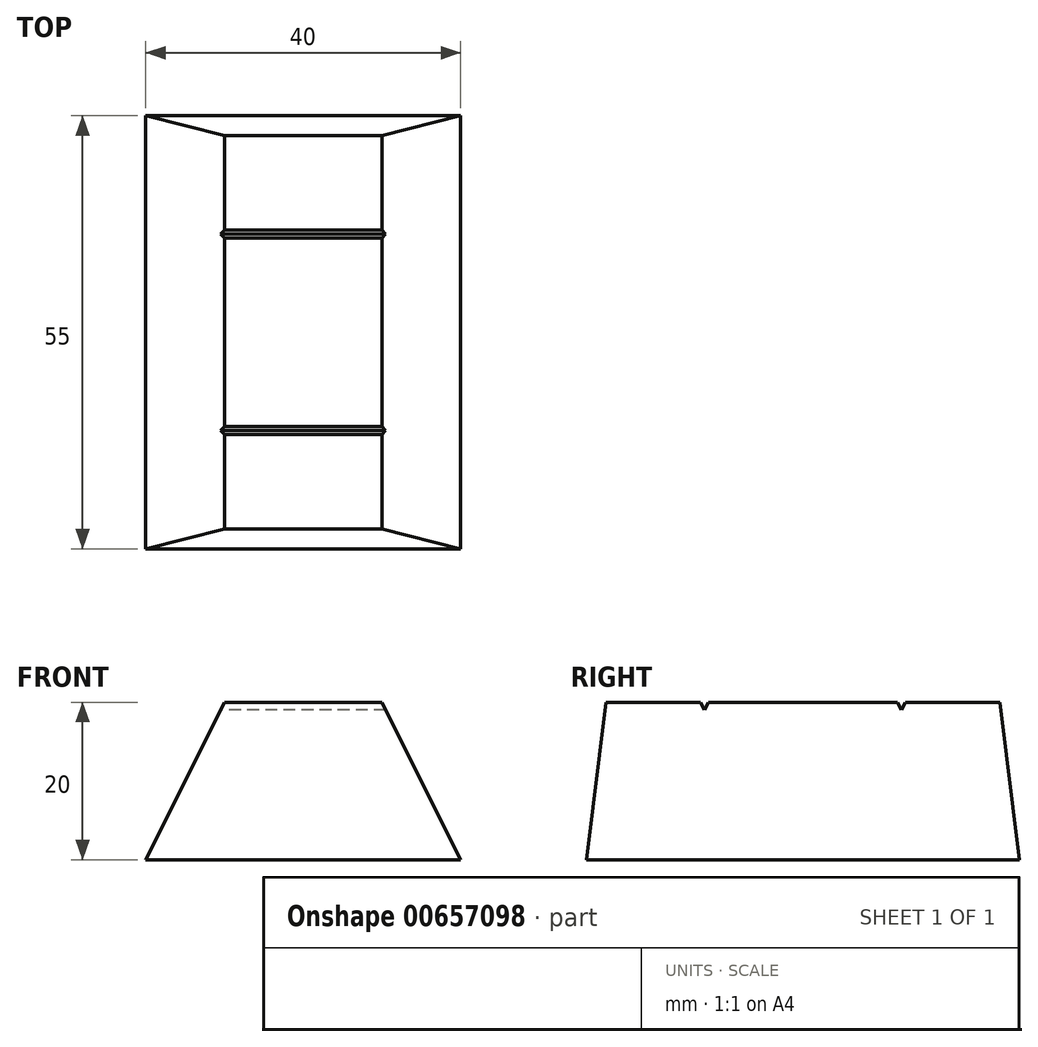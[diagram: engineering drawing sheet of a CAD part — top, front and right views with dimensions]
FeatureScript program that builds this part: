
annotation { "Feature Type Name" : "Feature", "Feature Type Description" : "" }
export const myFeature = defineFeature(function(context is Context, id is Id, definition is map)
    precondition{}
    {
        {
            var Q0;
            Q0=qCreatedBy(makeId("Front.planeOp"),FACE);
            var sketch = newSketch(context, id + "F0", { "sketchPlane" : qUnion([Q0])});
            skLineSegment(sketch, "E0.bottom", {"start": v(10, 10) * mm, "end": v(-10, 10) * mm});
            skLineSegment(sketch, "E0.top", {"start": v(10, -10) * mm, "end": v(-10, -10) * mm});
            skLineSegment(sketch, "E0.left", {"start": v(10, 10) * mm, "end": v(10, -10) * mm});
            skLineSegment(sketch, "E0.right", {"start": v(-10, 10) * mm, "end": v(-10, -10) * mm});
            skPoint(sketch, "E0.middle", {"position": v(0, 0) * mm});
            skLineSegment(sketch, "E1", {"start": v(10, -10) * mm, "end": v(20, -10) * mm});
            skLineSegment(sketch, "E2", {"start": v(20, -10) * mm, "end": v(10, 10) * mm});
            skLineSegment(sketch, "E3", {"start": v(-10, -10) * mm, "end": v(-20, -10) * mm});
            skLineSegment(sketch, "E4", {"start": v(-20, -10) * mm, "end": v(-10, 10) * mm});
            skLineSegment(sketch, "E5", {"start": v(-10, 10) * mm, "end": v(-20, 10) * mm});
            skLineSegment(sketch, "E6", {"start": v(-20, 10) * mm, "end": v(-20, -10) * mm});
            skLineSegment(sketch, "E7", {"start": v(20, -10) * mm, "end": v(20, 10) * mm});
            skLineSegment(sketch, "E8", {"start": v(20, 10) * mm, "end": v(10, 10) * mm});
            skSolve(sketch);
        }
        {
            var Q0;
            Q0 = qSketchRegion(id + "F0", true);
            extrude(context, id + "F1", {"entities" : qUnion([Q0]), "endBound" : BoundingType.SYMMETRIC, "depth" : 50 * mm, "offsetDistance" : 25.4 * mm});
        }
        {
            var Q0;
            Q0=qCreatedBy(makeId("Right.planeOp"),FACE);
            var sketch = newSketch(context, id + "F2", { "sketchPlane" : qUnion([Q0])});
            skLineSegment(sketch, "E9", {"start": v(0, 0) * mm, "end": v(25, 0) * mm});
            skLineSegment(sketch, "E10", {"start": v(0, 0) * mm, "end": v(-25, 0) * mm});
            skLineSegment(sketch, "E11", {"start": v(-25, 0) * mm, "end": v(-25, 10) * mm});
            skLineSegment(sketch, "E12", {"start": v(-25, 10) * mm, "end": v(25, 10) * mm});
            skLineSegment(sketch, "E13", {"start": v(25, 10) * mm, "end": v(25, 0) * mm});
            skLineSegment(sketch, "E14", {"start": v(-25, 0) * mm, "end": v(-25, -10) * mm});
            skLineSegment(sketch, "E15", {"start": v(25, 0) * mm, "end": v(25, -10) * mm});
            skLineSegment(sketch, "E16", {"start": v(25, -10) * mm, "end": v(27.5, -10) * mm});
            skLineSegment(sketch, "E17", {"start": v(27.5, -10) * mm, "end": v(25, 10) * mm});
            skLineSegment(sketch, "E18", {"start": v(-25, -10) * mm, "end": v(-27.5, -10) * mm});
            skLineSegment(sketch, "E19", {"start": v(-27.5, -10) * mm, "end": v(-25, 10) * mm});
            skLineSegment(sketch, "E20", {"start": v(-25, 10) * mm, "end": v(0, 10) * mm});
            skLineSegment(sketch, "E21", {"start": v(0, 10) * mm, "end": v(25, 10) * mm});
            skLineSegment(sketch, "E22", {"start": v(-12.5, 10) * mm, "end": v(0, 10) * mm});
            skLineSegment(sketch, "E23", {"start": v(12.5, 10) * mm, "end": v(0, 10) * mm});
            skLineSegment(sketch, "E24", {"start": v(-12.5, 10) * mm, "end": v(-12.5, 9) * mm});
            skLineSegment(sketch, "E25", {"start": v(12.5, 10) * mm, "end": v(12.5, 9) * mm});
            skLineSegment(sketch, "E26", {"start": v(-12.5, 10) * mm, "end": v(-13, 10) * mm});
            skLineSegment(sketch, "E27", {"start": v(-13, 10) * mm, "end": v(-12.5, 9) * mm});
            skLineSegment(sketch, "E28", {"start": v(-12.5, 10) * mm, "end": v(-12, 10) * mm});
            skLineSegment(sketch, "E29", {"start": v(-12, 10) * mm, "end": v(-12.5, 9) * mm});
            skLineSegment(sketch, "E30", {"start": v(12.5, 10) * mm, "end": v(12, 10) * mm});
            skLineSegment(sketch, "E31", {"start": v(12.5, 10) * mm, "end": v(13, 10) * mm});
            skLineSegment(sketch, "E32", {"start": v(13, 10) * mm, "end": v(12.5, 9) * mm});
            skLineSegment(sketch, "E33", {"start": v(12, 10) * mm, "end": v(12.5, 9) * mm});
            skSolve(sketch);
        }
        {
            var Q0;
            Q0=makeQuery(id+"F2.imprint","IMPRINT",FACE,{"disambiguationData":[TD([[makeQuery(id+"F2.imprint","IMPRINT",EDGE,{"derivedFrom":sQuery(id+"F2.wireOp",EDGE,"E11")}),1.0]])]});
            var Q1;
            Q1=makeQuery(id+"F2.imprint","IMPRINT",FACE,{"disambiguationData":[TD([[makeQuery(id+"F2.imprint","IMPRINT",EDGE,{"derivedFrom":sQuery(id+"F2.wireOp",EDGE,"E13")}),1.0]])]});
            extrude(context, id + "F3", {"entities" : qUnion([Q0, Q1]), "operationType" : NewBodyOperationType.ADD, "endBound" : BoundingType.SYMMETRIC, "depth" : 40 * mm, "offsetDistance" : 25 * mm});
        }
        {
            var Q0;
            Q0=makeQuery(id+"F0.imprint","IMPRINT",FACE,{"disambiguationData":[TD([[makeQuery(id+"F0.imprint","IMPRINT",EDGE,{"derivedFrom":sQuery(id+"F0.wireOp",EDGE,"E2")}),-1.0]])]});
            var Q1;
            Q1=makeQuery(id+"F0.imprint","IMPRINT",FACE,{"disambiguationData":[TD([[makeQuery(id+"F0.imprint","IMPRINT",EDGE,{"derivedFrom":sQuery(id+"F0.wireOp",EDGE,"E4")}),1.0]])]});
            extrude(context, id + "F4", {"entities" : qUnion([Q0, Q1]), "operationType" : NewBodyOperationType.REMOVE, "endBound" : BoundingType.SYMMETRIC, "oppositeDirection" : true, "depth" : 60 * mm, "offsetDistance" : 25 * mm});
        }
        {
            var Q0;
            Q0=makeQuery(id+"F2.imprint","IMPRINT",FACE,{"disambiguationData":[TD([[makeQuery(id+"F2.imprint","IMPRINT",EDGE,{"derivedFrom":sQuery(id+"F2.wireOp",EDGE,"E25")}),-1.0]])]});
            var Q1;
            Q1=makeQuery(id+"F2.imprint","IMPRINT",FACE,{"disambiguationData":[TD([[makeQuery(id+"F2.imprint","IMPRINT",EDGE,{"derivedFrom":sQuery(id+"F2.wireOp",EDGE,"E25")}),1.0]])]});
            var Q2;
            Q2=makeQuery(id+"F2.imprint","IMPRINT",FACE,{"disambiguationData":[TD([[makeQuery(id+"F2.imprint","IMPRINT",EDGE,{"derivedFrom":sQuery(id+"F2.wireOp",EDGE,"E24")}),-1.0]])]});
            var Q3;
            Q3=makeQuery(id+"F2.imprint","IMPRINT",FACE,{"disambiguationData":[TD([[makeQuery(id+"F2.imprint","IMPRINT",EDGE,{"derivedFrom":sQuery(id+"F2.wireOp",EDGE,"E24")}),1.0]])]});
            extrude(context, id + "F5", {"entities" : qUnion([Q0, Q1, Q2, Q3]), "operationType" : NewBodyOperationType.REMOVE, "endBound" : BoundingType.SYMMETRIC, "depth" : 50 * mm, "offsetDistance" : 25 * mm});
        }
    });
